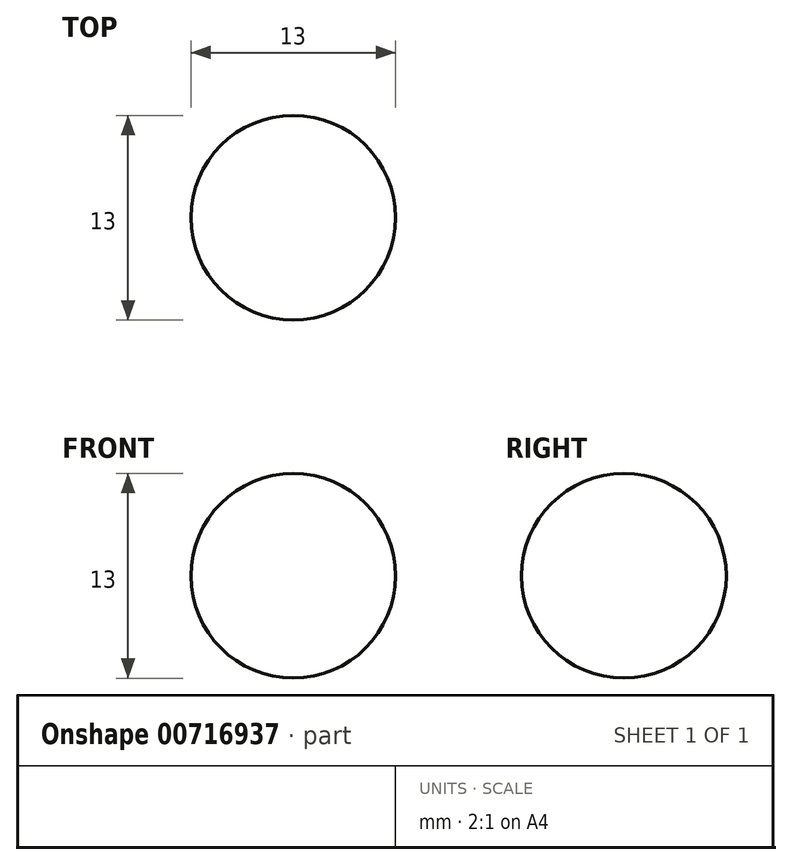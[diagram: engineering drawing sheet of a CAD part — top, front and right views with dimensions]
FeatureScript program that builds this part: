
annotation { "Feature Type Name" : "Feature", "Feature Type Description" : "" }
export const myFeature = defineFeature(function(context is Context, id is Id, definition is map)
    precondition{}
    {
        {
            var Q0;
            Q0=qCreatedBy(makeId("Front.planeOp"),FACE);
            var sketch = newSketch(context, id + "F0", { "sketchPlane" : qUnion([Q0])});
            skLineSegment(sketch, "E0", {"start": v(0, -5.53) * mm, "end": v(0, 7.47) * mm});
            skArc(sketch, "E1", {"start": v(0, 7.47) * mm, "mid": v(6.5, 0.97) * mm, "end": v(0, -5.53) * mm});
            skSolve(sketch);
        }
        {
            var Q0;
            Q0=makeQuery(id+"F0.imprint","IMPRINT",FACE,{"disambiguationData":[TD([[makeQuery(id+"F0.imprint","IMPRINT",EDGE,{"derivedFrom":sQuery(id+"F0.wireOp",EDGE,"E0")}),-1.0]])]});
            var Q1;
            Q1=sQuery(id+"F0.wireOp",EDGE,"E0");
            revolve(context, id + "F1", {"surfaceOperationType" : NewSurfaceOperationType.NEW, "entities" : qUnion([Q0]), "axis" : qUnion([Q1]), "revolveType" : RevolveType.FULL});
        }
    });
